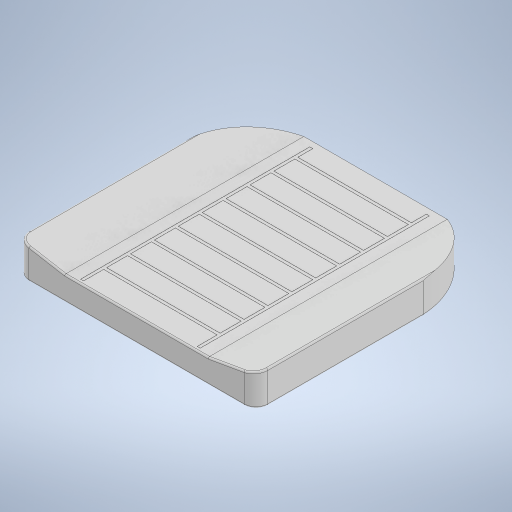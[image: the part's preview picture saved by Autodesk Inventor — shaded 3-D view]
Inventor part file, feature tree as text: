
AUTODESK INVENTOR PART (.ipt)
format: ipt  version: 2023 (Build 270158030, 158C)  size: 433,152 bytes
history: native  units: in
note: dims shown in document units (in); Inventor stores cm internally (conversion verified against a paired STEP export)
features: extrude x6, sketch x6, pattern_linear x1, hole x1, fillet x1
ambient origin geometry x8: Origin, YZ Plane, XZ Plane, XY Plane, X Axis, Y Axis, Z Axis, Center Point
bodies: Solid1 (feature_tree)
feature tree (15):
  extrude  "Extrusion1"  Depth=20.0in
  extrude  "Extrusion2"  Depth=1.0in
  extrude  "Extrusion3"  Depth=1.0in
  extrude  "Extrusion4"  Depth=2.0in TaperAngle=0.0deg
  extrude  "Extrusion5"  Depth=5.0in
  extrude  "Extrusion6"  Depth=0.125in
  pattern_linear  "Rectangular Pattern2"  Spacing1=0.25in  [1 undecoded]
  hole  "Hole1"  [1 undecoded]
  fillet  "Fillet3"  Radius=0.01in
  sketch  "Sketch1"  dims[d0=20.0in d1=20.0in]
  sketch  "Sketch2"  dims[d2=2.0in d3=0.0in d11=1.0in]
  sketch  "Sketch3"  dims[d12=1.0in d13=1.0in]
  sketch  "Sketch4"  dims[d14=1.0in d15=2.0in d16=0.0in]
  sketch  "Sketch6"  dims[d18=10.0in d19=5.0in]
  sketch  "Sketch7"  dims[d20=0.25in d21=5.0in d22=0.25in d25=0.01in d26=0.0in d29=0.01in d30=0.0in d34=90.0deg d35=90.0deg d36=9.75in d37=0.325in d39=5.0in d41=0.325in d42=0.0in d43=0.0in d44=1.675in d45=0.25in d46=9.5in d47=1.925in d48=9.5in d50=0.7in d51=0.0in d52=20.0in d53=0.0in d55=4.3307in d57=2.0in d58=6.5in d59=7.0in d60=0.5in d63=0.5in d65=0.5in d66=0.5in d67=0.5in d69=0.5in d70=0.196in d71=0.5in d72=0.375in d73=0.25in d74=0.5635in d75=0.75in d76=0.8108in d78=0.5in d79=0.5in d81=6.0in d83=7.0in d85=6.0in d86=7.0in d88=0.2929in d89=0.5in d90=0.5in d91=4.0in d92=4.0in d96=1.0in d97=0.125in d98=10.0in d99=6.5in d100=1.0in d101=1.0in d102=1.0in d103=0.5in d104=0.5in d105=0.5in d106=0.5in d107=1.0in]
note: 2 required parameter values undecoded (feature->parameter linkage not recoverable at this tier; creation-order binding heuristic only, values carry confidence <= 0.55)
